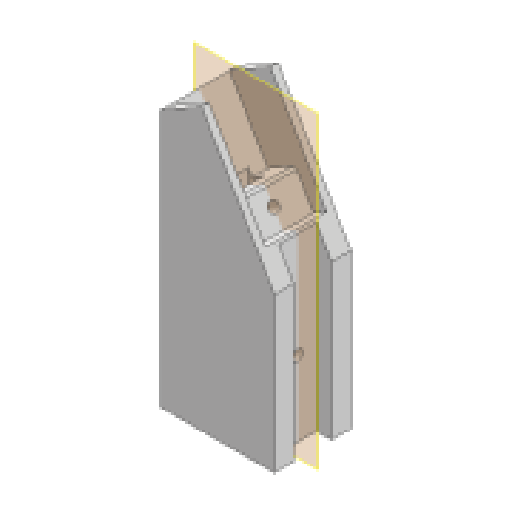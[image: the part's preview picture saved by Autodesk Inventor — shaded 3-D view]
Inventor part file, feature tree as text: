
AUTODESK INVENTOR PART (.ipt)
format: ipt  version: 2025.1 (Build 291241020, 241B)  size: 175,104 bytes
history: native  units: in
note: dims shown in document units (in); Inventor stores cm internally (conversion verified against a paired STEP export)
features: extrude x9, sketch x9, other x8, reference x6, plane x2, mirror x1, chamfer x1, projected_geometry x1
ambient origin geometry x8: Origin, YZ Plane, XZ Plane, XY Plane, X Axis, Y Axis, Z Axis, Center Point
bodies: Solid1 (feature_tree)
feature tree (37):
  extrude  "Extrusion1"  Depth=1.0in
  extrude  "Extrusion2"  Depth=3.4in
  plane  "Work Plane1"
  mirror  "Mirror1"
  extrude  "Extrusion3"  Depth=0.81in TaperAngle=0.0deg
  extrude  "Extrusion4"  Depth=0.5in
  extrude  "Extrusion5"  Depth=0.2in
  chamfer  "Chamfer1"  Distance=3.0in
  extrude  "Extrusion6"  Depth=0.487in
  plane  "Work Plane2"
  extrude  "Extrusion7"  Depth=0.2in TaperAngle=45.0deg
  extrude  "Extrusion8"  Depth=0.3in TaperAngle=0.0deg
  extrude  "Extrusion9"  Depth=0.4in TaperAngle=0.0deg
  sketch  "Sketch1"  dims[d0=0.618in d1=1.0in]
  sketch  "Sketch2"  dims[d2=1.5in d3=3.4in]
  projected_geometry  "Projected Loop1"
  sketch  "Sketch3"  dims[d4=120.0deg d5=0.81in d6=0.0in]
  sketch  "Sketch4"  dims[d7=0.1in d8=0.0in d9=0.5in]
  reference  "Reference1"
  sketch  "Sketch5"  dims[d10=0.25in d11=0.2in d12=3.0in d13=0.0in]
  sketch  "Sketch6"  dims[d14=0.6in d15=0.0in d16=0.487in]
  reference  "Reference2"
  sketch  "Sketch7"  dims[d17=0.2in d18=0.0in d19=0.04in d20=0.125in d21=45.0deg]
  sketch  "Sketch8"  dims[d22=0.14in d23=0.3in d24=0.0in]
  reference  "Reference3"
  reference  "Reference4"
  sketch  "Sketch9"  dims[d26=0.2in d27=0.4in d28=0.0in d29=0.6in d30=0.0in d31=0.6in d32=0.0in]
  reference  "Reference5"
  reference  "Reference6"
  parser-record x2  (decoder bookkeeping rows leaked as tree rows — omitted from the tree; the rows remain in map.json)
  other  "Finger Assem.iam"
  other  "KNUCKLE 3:1"
  other  "Servo Base:3"
  other  "Hand Assem.iam"
  other  "Palm:1"
  other  "Wrist Base:1"
note: 2 file-system paths scrubbed to <path> (originals preserved in map.json)
